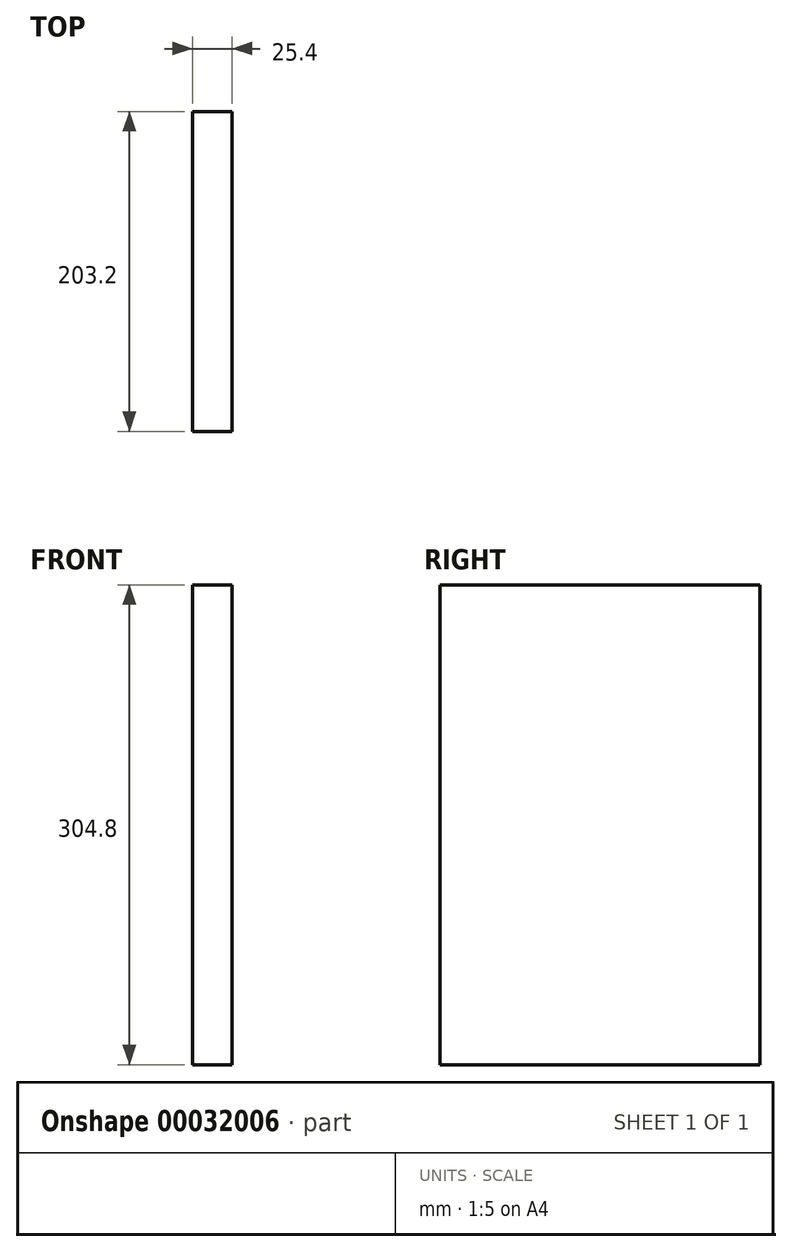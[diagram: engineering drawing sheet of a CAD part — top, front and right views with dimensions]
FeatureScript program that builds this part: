
annotation { "Feature Type Name" : "Feature", "Feature Type Description" : "" }
export const myFeature = defineFeature(function(context is Context, id is Id, definition is map)
    precondition{}
    {
        {
            var Q0;
            Q0=qCreatedBy(makeId("Right.planeOp"),FACE);
            var sketch = newSketch(context, id + "F0", { "sketchPlane" : qUnion([Q0])});
            skLineSegment(sketch, "E0.rect.bottom", {"start": v(101.6, -152.4) * mm, "end": v(-101.6, -152.4) * mm});
            skLineSegment(sketch, "E0.rect.top", {"start": v(101.6, 152.4) * mm, "end": v(-101.6, 152.4) * mm});
            skLineSegment(sketch, "E0.rect.left", {"start": v(101.6, -152.4) * mm, "end": v(101.6, 152.4) * mm});
            skLineSegment(sketch, "E0.rect.right", {"start": v(-101.6, -152.4) * mm, "end": v(-101.6, 152.4) * mm});
            skPoint(sketch, "E0.rect.middle", {"position": v(0, 0) * mm});
            skSolve(sketch);
        }
        {
            var Q0;
            Q0=makeQuery(id+"F0.imprint","IMPRINT",FACE,{"disambiguationData":[TD([[makeQuery(id+"F0.imprint","IMPRINT",EDGE,{"derivedFrom":sQuery(id+"F0.wireOp",EDGE,"E0.rect.bottom")}),-1.0]])]});
            extrude(context, id + "F1", {"entities" : qUnion([Q0]), "depth" : 25.4 * mm});
        }
    });
